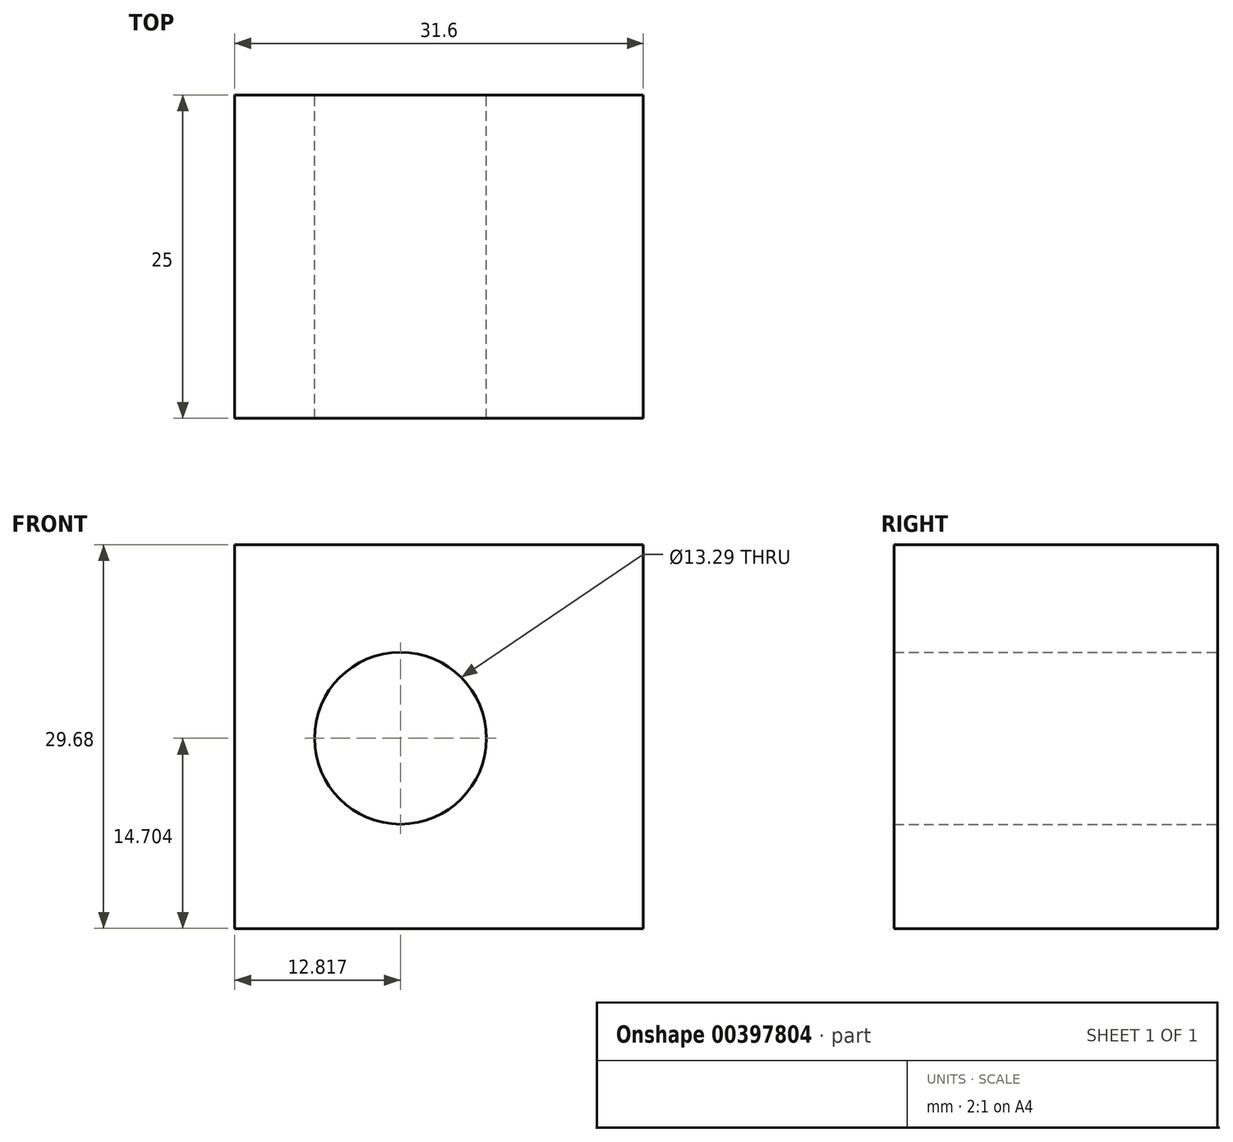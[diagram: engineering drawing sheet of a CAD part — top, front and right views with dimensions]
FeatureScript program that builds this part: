
annotation { "Feature Type Name" : "Feature", "Feature Type Description" : "" }
export const myFeature = defineFeature(function(context is Context, id is Id, definition is map)
    precondition{}
    {
        {
            var Q0;
            Q0=qCreatedBy(makeId("Front.planeOp"),FACE);
            var sketch = newSketch(context, id + "F0", { "sketchPlane" : qUnion([Q0])});
            skLineSegment(sketch, "E0.bottom", {"start": v(-33.44, 4.51) * mm, "end": v(-65.04, 4.51) * mm});
            skLineSegment(sketch, "E0.top", {"start": v(-33.44, -25.17) * mm, "end": v(-65.04, -25.17) * mm});
            skLineSegment(sketch, "E0.left", {"start": v(-33.44, 4.51) * mm, "end": v(-33.44, -25.17) * mm});
            skLineSegment(sketch, "E0.right", {"start": v(-65.04, 4.51) * mm, "end": v(-65.04, -25.17) * mm});
            skSolve(sketch);
        }
        {
            var Q0;
            Q0 = qSketchRegion(id + "F0", true);
            var sketch = newSketch(context, id + "F1", { "sketchPlane" : qUnion([Q0])});
            skCircle(sketch, "E1", {"center": v(-52.22, -10.47) * mm, "radius": 6.64 * mm});
            skSolve(sketch);
        }
        {
            var Q0;
            Q0=makeQuery(id+"F1.imprint","IMPRINT",FACE,{"disambiguationData":[TD([[makeQuery(id+"F1.imprint","IMPRINT",EDGE,{"derivedFrom":sQuery(id+"F1.wireOp",EDGE,"E1")}),-1.0]])]});
            extrude(context, id + "F2", {"entities" : qUnion([Q0]), "depth" : 25 * mm});
        }
    });
